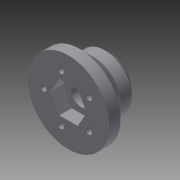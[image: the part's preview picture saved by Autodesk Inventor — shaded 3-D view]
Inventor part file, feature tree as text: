
AUTODESK INVENTOR PART (.ipt)
format: ipt  version: 2014 SP2 (Build 180246200, 246)  size: 154,112 bytes
history: native  units: mm
features: extrude x5, sketch x4, chamfer x2
ambient origin geometry x8: Origin, YZ Plane, XZ Plane, XY Plane, X Axis, Y Axis, Z Axis, Center Point
bodies: Solid1 (feature_tree)
feature tree (11):
  extrude  "Extrusion1"  Depth=22.2mm
  extrude  "Extrusion2"  Depth=2.7mm
  extrude  "Extrusion3"  Depth=2.7mm
  extrude  "Extrusion4"  Depth=5.0mm TaperAngle=0.0deg
  chamfer  "Chamfer1"  Distance=30.0mm
  extrude  "Extrusion5"  Depth=5.5mm TaperAngle=0.0deg
  chamfer  "Chamfer2"  Distance=14.0mm
  sketch  "Sketch1"  dims[d0=36.0mm d1=22.2mm]
  sketch  "Sketch3"  dims[d2=2.7mm d3=2.7mm]
  sketch  "Sketch4"  dims[d4=2.7mm d5=2.7mm]
  sketch  "Sketch5"  dims[d6=2.7mm d7=5.0mm d8=0.0mm d9=30.0mm d14=6.0mm d15=0.0mm d23=14.0mm d24=5.5mm d25=0.0mm d26=9.0mm d27=9.0mm d28=0.0mm d29=3.0mm d30=2.0mm d31=45.0deg d32=8.0mm d33=0.0mm d34=3.0mm d35=2.0mm d36=45.0deg]
